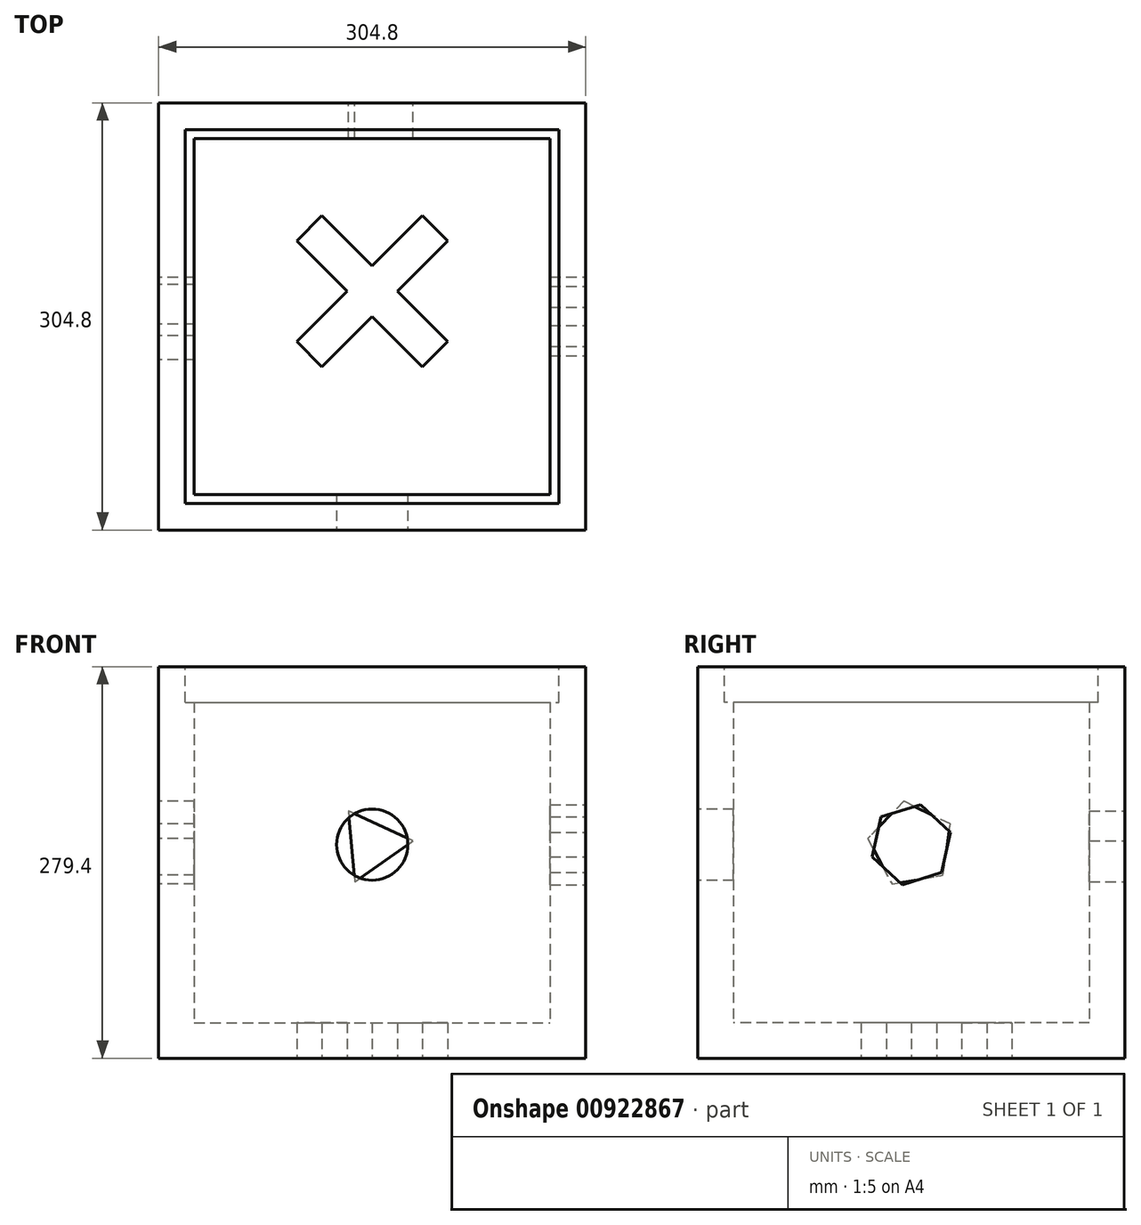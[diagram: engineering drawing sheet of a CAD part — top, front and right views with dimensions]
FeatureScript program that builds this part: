
annotation { "Feature Type Name" : "Feature", "Feature Type Description" : "" }
export const myFeature = defineFeature(function(context is Context, id is Id, definition is map)
    precondition{}
    {
        {
            var Q0;
            Q0=qCreatedBy(makeId("Top.planeOp"),FACE);
            var sketch = newSketch(context, id + "F0", { "sketchPlane" : qUnion([Q0])});
            skLineSegment(sketch, "E0.bottom", {"start": v(-170.96, 231.96) * mm, "end": v(133.84, 231.96) * mm});
            skLineSegment(sketch, "E0.top", {"start": v(-170.96, -72.84) * mm, "end": v(133.84, -72.84) * mm});
            skLineSegment(sketch, "E0.left", {"start": v(-170.96, 231.96) * mm, "end": v(-170.96, -72.84) * mm});
            skLineSegment(sketch, "E0.right", {"start": v(133.84, 231.96) * mm, "end": v(133.84, -72.84) * mm});
            skSolve(sketch);
        }
        {
            var Q0;
            Q0=makeQuery(id+"F0.imprint","IMPRINT",FACE,{"disambiguationData":[TD([[makeQuery(id+"F0.imprint","IMPRINT",EDGE,{"derivedFrom":sQuery(id+"F0.wireOp",EDGE,"E0.bottom")}),-1.0]])]});
            extrude(context, id + "F1", {"entities" : qUnion([Q0]), "depth" : 25.4 * mm, "offsetDistance" : 25.4 * mm});
        }
        {
            var Q0;
            Q0=makeQuery(id+"F1.opExtrude","CAP_FACE",FACE,{"disambiguationData":[OSD([sQuery(id+"F0.wireOp",EDGE,"E0.bottom"),sQuery(id+"F0.wireOp",EDGE,"E0.top"),sQuery(id+"F0.wireOp",EDGE,"E0.left"),sQuery(id+"F0.wireOp",EDGE,"E0.right")])],"isStart":false});
            var sketch = newSketch(context, id + "F2", { "sketchPlane" : qUnion([Q0])});
            skLineSegment(sketch, "E1.bottom", {"start": v(-170.96, 231.96) * mm, "end": v(133.84, 231.96) * mm});
            skLineSegment(sketch, "E1.left", {"start": v(-170.96, 231.96) * mm, "end": v(-170.96, -72.84) * mm});
            skLineSegment(sketch, "E1.right", {"start": v(133.84, 231.96) * mm, "end": v(133.84, -72.84) * mm});
            skLineSegment(sketch, "E2", {"start": v(-170.96, 231.96) * mm, "end": v(-145.56, 231.96) * mm});
            skLineSegment(sketch, "E3", {"start": v(-145.56, 231.96) * mm, "end": v(-145.56, 206.56) * mm});
            skLineSegment(sketch, "E4", {"start": v(133.84, -72.84) * mm, "end": v(108.44, -72.84) * mm});
            skLineSegment(sketch, "E5", {"start": v(108.44, -72.84) * mm, "end": v(108.44, -47.44) * mm});
            skLineSegment(sketch, "E6", {"start": v(-170.96, -72.84) * mm, "end": v(133.84, -72.84) * mm});
            skLineSegment(sketch, "E7.bottom", {"start": v(-145.56, 206.56) * mm, "end": v(108.44, 206.56) * mm});
            skLineSegment(sketch, "E7.top", {"start": v(-145.56, -47.44) * mm, "end": v(108.44, -47.44) * mm});
            skLineSegment(sketch, "E7.left", {"start": v(-145.56, 206.56) * mm, "end": v(-145.56, -47.44) * mm});
            skLineSegment(sketch, "E7.right", {"start": v(108.44, 206.56) * mm, "end": v(108.44, -47.44) * mm});
            skSolve(sketch);
        }
        {
            var Q0;
            {var subQ1=sQuery(id+"F2.wireOp",EDGE,"E1.left");Q0=makeQuery(id+"F2.imprint","IMPRINT",FACE,{"disambiguationData":[TD([[makeQuery(id+"F2.imprint","IMPRINT",EDGE,{"derivedFrom":subQ1}),1.0]])]});}
            var Q1;
            Q1=makeQuery(id+"F2.imprint","IMPRINT",FACE,{"disambiguationData":[TD([[makeQuery(id+"F2.imprint","IMPRINT",EDGE,{"derivedFrom":sQuery(id+"F2.wireOp",EDGE,"E1.bottom")}),-1.0]])]});
            extrude(context, id + "F3", {"entities" : qUnion([Q0, Q1]), "operationType" : NewBodyOperationType.ADD, "depth" : 254 * mm, "offsetDistance" : 25.4 * mm});
        }
        {
            var Q0;
            Q0=makeQuery(id+"F3.opExtrude","CAP_FACE",FACE,{"disambiguationData":[OSD([sQuery(id+"F2.wireOp",EDGE,"E1.bottom"),sQuery(id+"F2.wireOp",EDGE,"E1.left"),sQuery(id+"F2.wireOp",EDGE,"E1.right"),sQuery(id+"F2.wireOp",EDGE,"E2"),sQuery(id+"F2.wireOp",EDGE,"E6"),sQuery(id+"F2.wireOp",EDGE,"E7.bottom"),sQuery(id+"F2.wireOp",EDGE,"E7.top"),sQuery(id+"F2.wireOp",EDGE,"E7.left"),sQuery(id+"F2.wireOp",EDGE,"E7.right")])],"isStart":false});
            var sketch = newSketch(context, id + "F4", { "sketchPlane" : qUnion([Q0])});
            skLineSegment(sketch, "E8", {"start": v(-145.56, 206.56) * mm, "end": v(-145.56, 212.9) * mm});
            skLineSegment(sketch, "E9", {"start": v(-145.56, 212.9) * mm, "end": v(-151.91, 212.9) * mm});
            skLineSegment(sketch, "E10", {"start": v(108.44, -47.44) * mm, "end": v(108.44, -53.8) * mm});
            skLineSegment(sketch, "E11", {"start": v(108.44, -53.8) * mm, "end": v(114.79, -53.8) * mm});
            skLineSegment(sketch, "E12.bottom", {"start": v(-151.91, 212.9) * mm, "end": v(114.79, 212.9) * mm});
            skLineSegment(sketch, "E12.top", {"start": v(-151.91, -53.8) * mm, "end": v(114.79, -53.8) * mm});
            skLineSegment(sketch, "E12.left", {"start": v(-151.91, 212.9) * mm, "end": v(-151.91, -53.8) * mm});
            skLineSegment(sketch, "E12.right", {"start": v(114.79, 212.9) * mm, "end": v(114.79, -53.8) * mm});
            skSolve(sketch);
        }
        {
            var Q0;
            {var subQ1=sQuery(id+"F4.wireOp",EDGE,"E8");Q0=makeQuery(id+"F4.imprint","IMPRINT",FACE,{"disambiguationData":[TD([[makeQuery(id+"F4.imprint","IMPRINT",EDGE,{"derivedFrom":subQ1}),-1.0]])]});}
            var Q1;
            {var subQ4=sQuery(id+"F4.wireOp",EDGE,"E8");Q1=makeQuery(id+"F4.imprint","IMPRINT",FACE,{"disambiguationData":[TD([[makeQuery(id+"F4.imprint","IMPRINT",EDGE,{"derivedFrom":subQ4}),1.0]])]});}
            extrude(context, id + "F5", {"entities" : qUnion([Q0, Q1]), "operationType" : NewBodyOperationType.REMOVE, "oppositeDirection" : true, "depth" : 25.4 * mm, "offsetDistance" : 25.4 * mm});
        }
        {
            var Q0;
            Q0=makeQuery(id+"F3.boolean.opBoolean","MERGE",FACE,{"derivedFrom":[makeQuery(id+"F1.opExtrude","SWEPT_FACE",FACE,{"disambiguationData":[OSD([sQuery(id+"F0.wireOp",EDGE,"E0.top")])]}),makeQuery(id+"F3.opExtrude","SWEPT_FACE",FACE,{"disambiguationData":[OSD([sQuery(id+"F2.wireOp",EDGE,"E6")])]})]});
            var sketch = newSketch(context, id + "F6", { "sketchPlane" : qUnion([Q0])});
            skLineSegment(sketch, "E13", {"start": v(-170.96, 279.4) * mm, "end": v(-18.56, 279.4) * mm});
            skLineSegment(sketch, "E14", {"start": v(-18.56, 279.4) * mm, "end": v(-18.56, 152.4) * mm});
            skCircle(sketch, "E15", {"center": v(-18.56, 152.4) * mm, "radius": 25.4 * mm});
            skSolve(sketch);
        }
        {
            var Q0;
            Q0=makeQuery(id+"F6.imprint","IMPRINT",FACE,{"disambiguationData":[TD([[makeQuery(id+"F6.imprint","IMPRINT",EDGE,{"derivedFrom":sQuery(id+"F6.wireOp",EDGE,"E15")}),1.0]])]});
            extrude(context, id + "F7", {"entities" : qUnion([Q0]), "operationType" : NewBodyOperationType.REMOVE, "oppositeDirection" : true, "depth" : 25.4 * mm, "offsetDistance" : 25.4 * mm});
        }
        {
            var Q0;
            Q0=makeQuery(id+"F3.boolean.opBoolean","MERGE",FACE,{"derivedFrom":[makeQuery(id+"F1.opExtrude","SWEPT_FACE",FACE,{"disambiguationData":[OSD([sQuery(id+"F0.wireOp",EDGE,"E0.right")])]}),makeQuery(id+"F3.opExtrude","SWEPT_FACE",FACE,{"disambiguationData":[OSD([sQuery(id+"F2.wireOp",EDGE,"E1.right")])]})]});
            var sketch = newSketch(context, id + "F8", { "sketchPlane" : qUnion([Q0])});
            skLineSegment(sketch, "E16", {"start": v(-72.84, 279.4) * mm, "end": v(79.56, 279.4) * mm});
            skLineSegment(sketch, "E17", {"start": v(79.56, 279.4) * mm, "end": v(79.56, 152.4) * mm});
            skCircle(sketch, "E18.cCircle", {"center": v(79.56, 152.4) * mm, "radius": 25.4 * mm, "construction": true});
            skLineSegment(sketch, "E18.0", {"start": v(107.57, 161.1) * mm, "end": v(101.1, 132.5) * mm});
            skLineSegment(sketch, "E18.1", {"start": v(101.1, 132.5) * mm, "end": v(73.08, 123.8) * mm});
            skLineSegment(sketch, "E18.2", {"start": v(73.08, 123.8) * mm, "end": v(51.55, 143.7) * mm});
            skLineSegment(sketch, "E18.3", {"start": v(51.55, 143.7) * mm, "end": v(58.02, 172.3) * mm});
            skLineSegment(sketch, "E18.4", {"start": v(58.02, 172.3) * mm, "end": v(86.03, 181) * mm});
            skLineSegment(sketch, "E18.5", {"start": v(86.03, 181) * mm, "end": v(107.57, 161.1) * mm});
            skPoint(sketch, "E18.0.midPoint", {"position": v(104.33, 146.8) * mm});
            skSolve(sketch);
        }
        {
            var Q0;
            Q0=makeQuery(id+"F8.imprint","IMPRINT",FACE,{"disambiguationData":[TD([[makeQuery(id+"F8.imprint","IMPRINT",EDGE,{"derivedFrom":sQuery(id+"F8.wireOp",EDGE,"E18.0")}),-1.0]])]});
            extrude(context, id + "F9", {"entities" : qUnion([Q0]), "operationType" : NewBodyOperationType.REMOVE, "oppositeDirection" : true, "depth" : 25.4 * mm, "offsetDistance" : 25.4 * mm});
        }
        {
            var Q0;
            Q0=makeQuery(id+"F3.boolean.opBoolean","MERGE",FACE,{"derivedFrom":[makeQuery(id+"F1.opExtrude","SWEPT_FACE",FACE,{"disambiguationData":[OSD([sQuery(id+"F0.wireOp",EDGE,"E0.bottom")])]}),makeQuery(id+"F3.opExtrude","SWEPT_FACE",FACE,{"disambiguationData":[OSD([sQuery(id+"F2.wireOp",EDGE,"E1.bottom"),sQuery(id+"F2.wireOp",EDGE,"E2")])]})]});
            var sketch = newSketch(context, id + "F10", { "sketchPlane" : qUnion([Q0])});
            skLineSegment(sketch, "E19", {"start": v(-133.84, 279.4) * mm, "end": v(18.56, 279.4) * mm});
            skLineSegment(sketch, "E20", {"start": v(18.56, 279.4) * mm, "end": v(18.56, 152.4) * mm});
            skCircle(sketch, "E21.cCircle", {"center": v(18.56, 152.4) * mm, "radius": 14.66 * mm, "construction": true});
            skLineSegment(sketch, "E21.0", {"start": v(35.44, 176.39) * mm, "end": v(30.9, 125.8) * mm});
            skLineSegment(sketch, "E21.1", {"start": v(30.9, 125.8) * mm, "end": v(-10.65, 155.02) * mm});
            skLineSegment(sketch, "E21.2", {"start": v(-10.65, 155.02) * mm, "end": v(35.44, 176.39) * mm});
            skPoint(sketch, "E21.0.midPoint", {"position": v(33.17, 151.1) * mm});
            skSolve(sketch);
        }
        {
            var Q0;
            {var subQ0=sQuery(id+"F10.wireOp",EDGE,"E21.0");Q0=makeQuery(id+"F10.imprint","IMPRINT",FACE,{"disambiguationData":[TD([[makeQuery(id+"F10.imprint","IMPRINT",EDGE,{"derivedFrom":subQ0}),-1.0]])]});}
            extrude(context, id + "F11", {"entities" : qUnion([Q0]), "operationType" : NewBodyOperationType.REMOVE, "oppositeDirection" : true, "depth" : 25.4 * mm, "offsetDistance" : 25.4 * mm});
        }
        {
            var Q0;
            Q0=makeQuery(id+"F1.opExtrude","CAP_FACE",FACE,{"disambiguationData":[OSD([sQuery(id+"F0.wireOp",EDGE,"E0.bottom"),sQuery(id+"F0.wireOp",EDGE,"E0.top"),sQuery(id+"F0.wireOp",EDGE,"E0.left"),sQuery(id+"F0.wireOp",EDGE,"E0.right")])],"isStart":true});
            var sketch = newSketch(context, id + "F12", { "sketchPlane" : qUnion([Q0])});
            skLineSegment(sketch, "E22", {"start": v(-170.96, 72.84) * mm, "end": v(-18.56, 72.84) * mm});
            skLineSegment(sketch, "E23", {"start": v(-18.56, 72.84) * mm, "end": v(-18.56, -79.56) * mm});
            skLineSegment(sketch, "E24", {"start": v(-18.56, -79.56) * mm, "end": v(17.36, -43.64) * mm});
            skLineSegment(sketch, "E25", {"start": v(17.36, -43.64) * mm, "end": v(35.32, -61.6) * mm});
            skLineSegment(sketch, "E26", {"start": v(35.32, -61.6) * mm, "end": v(-0.6, -97.52) * mm});
            skLineSegment(sketch, "E27", {"start": v(-0.6, -97.52) * mm, "end": v(35.32, -133.44) * mm});
            skLineSegment(sketch, "E28", {"start": v(35.32, -133.44) * mm, "end": v(17.36, -151.4) * mm});
            skLineSegment(sketch, "E29", {"start": v(17.36, -151.4) * mm, "end": v(-18.56, -115.48) * mm});
            skLineSegment(sketch, "E30", {"start": v(-18.56, -115.48) * mm, "end": v(-54.48, -151.4) * mm});
            skLineSegment(sketch, "E31", {"start": v(-54.48, -151.4) * mm, "end": v(-72.44, -133.44) * mm});
            skLineSegment(sketch, "E32", {"start": v(-72.44, -133.44) * mm, "end": v(-36.52, -97.52) * mm});
            skLineSegment(sketch, "E33", {"start": v(-36.52, -97.52) * mm, "end": v(-72.44, -61.6) * mm});
            skLineSegment(sketch, "E34", {"start": v(-72.44, -61.6) * mm, "end": v(-54.48, -43.64) * mm});
            skLineSegment(sketch, "E35", {"start": v(-54.48, -43.64) * mm, "end": v(-18.56, -79.56) * mm});
            skSolve(sketch);
        }
        {
            var Q0;
            Q0=makeQuery(id+"F12.imprint","IMPRINT",FACE,{"disambiguationData":[TD([[makeQuery(id+"F12.imprint","IMPRINT",EDGE,{"derivedFrom":sQuery(id+"F12.wireOp",EDGE,"E24")}),-1.0]])]});
            extrude(context, id + "F13", {"entities" : qUnion([Q0]), "operationType" : NewBodyOperationType.REMOVE, "oppositeDirection" : true, "depth" : 25.4 * mm, "offsetDistance" : 25.4 * mm});
        }
        {
            var Q0;
            Q0=makeQuery(id+"F3.boolean.opBoolean","MERGE",FACE,{"derivedFrom":[makeQuery(id+"F1.opExtrude","SWEPT_FACE",FACE,{"disambiguationData":[OSD([sQuery(id+"F0.wireOp",EDGE,"E0.left")])]}),makeQuery(id+"F3.opExtrude","SWEPT_FACE",FACE,{"disambiguationData":[OSD([sQuery(id+"F2.wireOp",EDGE,"E1.left")])]})]});
            var sketch = newSketch(context, id + "F14", { "sketchPlane" : qUnion([Q0])});
            skLineSegment(sketch, "E36", {"start": v(-231.96, 279.4) * mm, "end": v(-79.56, 279.4) * mm});
            skLineSegment(sketch, "E37", {"start": v(-79.56, 279.4) * mm, "end": v(-79.56, 152.4) * mm});
            skCircle(sketch, "E38.cCircle", {"center": v(-79.56, 152.4) * mm, "radius": 25.4 * mm, "construction": true});
            skLineSegment(sketch, "E38.0", {"start": v(-48.47, 156.8) * mm, "end": v(-65.76, 124.2) * mm});
            skLineSegment(sketch, "E38.1", {"start": v(-65.76, 124.2) * mm, "end": v(-102.12, 130.56) * mm});
            skLineSegment(sketch, "E38.2", {"start": v(-102.12, 130.56) * mm, "end": v(-107.3, 167.1) * mm});
            skLineSegment(sketch, "E38.3", {"start": v(-107.3, 167.1) * mm, "end": v(-74.14, 183.33) * mm});
            skLineSegment(sketch, "E38.4", {"start": v(-74.14, 183.33) * mm, "end": v(-48.47, 156.8) * mm});
            skPoint(sketch, "E38.0.midPoint", {"position": v(-57.12, 140.5) * mm});
            skSolve(sketch);
        }
        {
            var Q0;
            Q0=makeQuery(id+"F14.imprint","IMPRINT",FACE,{"disambiguationData":[TD([[makeQuery(id+"F14.imprint","IMPRINT",EDGE,{"derivedFrom":sQuery(id+"F14.wireOp",EDGE,"E38.0")}),-1.0]])]});
            extrude(context, id + "F15", {"entities" : qUnion([Q0]), "operationType" : NewBodyOperationType.REMOVE, "oppositeDirection" : true, "depth" : 25.4 * mm, "offsetDistance" : 25.4 * mm});
        }
    });
